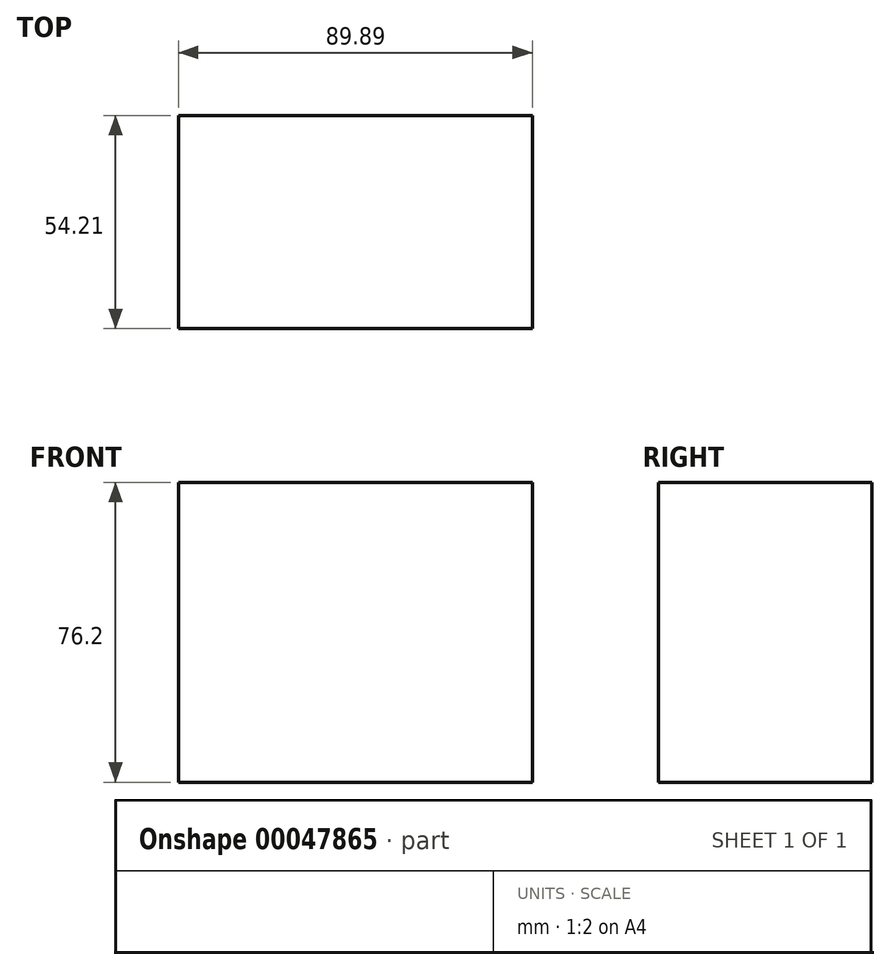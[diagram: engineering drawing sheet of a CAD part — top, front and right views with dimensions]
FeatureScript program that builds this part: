
annotation { "Feature Type Name" : "Feature", "Feature Type Description" : "" }
export const myFeature = defineFeature(function(context is Context, id is Id, definition is map)
    precondition{}
    {
        {
            var Q0;
            Q0=qCreatedBy(makeId("Top.planeOp"),FACE);
            var sketch = newSketch(context, id + "F0", { "sketchPlane" : qUnion([Q0])});
            skLineSegment(sketch, "E0.bottom", {"start": v(-55.22, 26.28) * mm, "end": v(34.67, 26.28) * mm});
            skLineSegment(sketch, "E0.top", {"start": v(-55.22, -27.93) * mm, "end": v(34.67, -27.93) * mm});
            skLineSegment(sketch, "E0.left", {"start": v(-55.22, 26.28) * mm, "end": v(-55.22, -27.93) * mm});
            skLineSegment(sketch, "E0.right", {"start": v(34.67, 26.28) * mm, "end": v(34.67, -27.93) * mm});
            skSolve(sketch);
        }
        {
            var Q0;
            Q0=makeQuery(id+"F0.imprint","IMPRINT",FACE,{"disambiguationData":[TD([[makeQuery(id+"F0.imprint","IMPRINT",EDGE,{"derivedFrom":sQuery(id+"F0.wireOp",EDGE,"E0.bottom")}),-1.0]])]});
            extrude(context, id + "F1", {"entities" : qUnion([Q0]), "depth" : 76.2 * mm});
        }
    });
